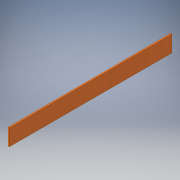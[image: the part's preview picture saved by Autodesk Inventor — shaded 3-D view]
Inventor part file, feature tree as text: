
AUTODESK INVENTOR PART (.ipt)
format: ipt  version: 2016 (Build 200138000, 138)  size: 94,720 bytes
history: native  units: in
note: dims shown in document units (in); Inventor stores cm internally (conversion verified against a paired STEP export)
features: extrude x1, sketch x1
ambient origin geometry x8: Origin, YZ Plane, XZ Plane, XY Plane, X Axis, Y Axis, Z Axis, Center Point
bodies: Solid1 (feature_tree)
feature tree (2):
  extrude  "Extrusion1"  Depth=6.5in
  sketch  "Sketch1"  dims[d0=64.0in d1=6.5in d2=0.4375in d3=0.0in]
